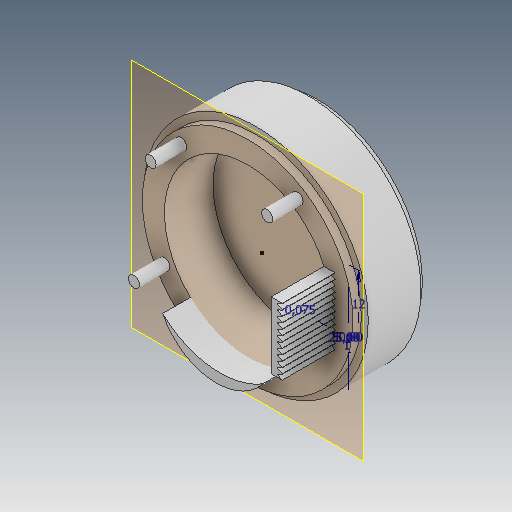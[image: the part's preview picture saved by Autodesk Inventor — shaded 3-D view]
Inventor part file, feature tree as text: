
AUTODESK INVENTOR PART (.ipt)
format: ipt  version: 2020.3 (Build 243373010, 373A)  size: 434,176 bytes
history: native  units: mm
features: extrude x11, sketch x11, plane x4, projected_geometry x3, pattern_linear x1, fillet x1
ambient origin geometry x8: Origin, YZ Plane, XZ Plane, XY Plane, X Axis, Y Axis, Z Axis, Center Point
bodies: Solid1 (feature_tree)
feature tree (31):
  extrude  "Extrusion1"  Depth=12.5mm TaperAngle=0.0deg
  extrude  "Extrusion2"  Depth=1.5mm TaperAngle=0.0deg
  extrude  "Extrusion3"  Depth=30.0mm
  extrude  "Extrusion4"  Depth=8.75mm
  extrude  "Extrusion5"  Depth=2.0mm
  plane  "Work Plane1"
  sketch  "Sketch7"  dims[d17=2.0mm d18=2.0mm]
  extrude  "Extrusion6"  Depth=2.0mm
  extrude  "Extrusion8"  Depth=12.0mm
  sketch  "Sketch10"  dims[d21=9.0mm d22=8.0mm]
  plane  "Work Plane2"
  plane  "Work Plane3"
  sketch  "Sketch14"  dims[d23=12.25mm d24=14.25mm]
  plane  "Work Plane4"
  sketch  "Sketch15"  dims[d25=5.5mm d26=0.0mm d29=10.0mm]
  extrude  "Extrusion13"  Depth=9.0mm
  extrude  "Extrusion14"  Depth=14.25mm
  extrude  "Extrusion15"  Depth=10.0mm
  pattern_linear  "Rectangular Pattern2"  Spacing1=4.363323mm  [1 undecoded]
  extrude  "Extrusion16"  Depth=1.0mm
  fillet  "Fillet1"  Radius=0.075mm
  sketch  "Sketch1"  dims[d0=40.45mm d3=12.5mm d4=0.0mm]
  sketch  "Sketch2"  dims[d6=1.25mm d7=1.5mm d8=0.0mm]
  projected_geometry  "Projected Loop1"
  sketch  "Sketch3"  dims[d9=40.45mm d10=30.0mm]
  sketch  "Sketch4"  dims[d11=8.75mm d12=0.0mm d13=1.25mm]
  sketch  "Sketch5"  dims[d14=1.5mm d15=0.0mm d16=2.0mm]
  sketch  "Sketch8"  dims[d19=15.0mm d20=12.0mm]
  projected_geometry  "Projected Loop3"
  sketch  "Sketch16"  dims[d31=12.0mm d32=3.5mm d33=0.0mm d34=4.363323mm d36=1.0mm d38=0.075mm d39=8.726646mm d40=120.0mm d42=1.0mm d43=10.0mm d45=10.0mm d49=10.75mm d50=5.0mm d51=0.0mm d53=15.0mm d54=7.5mm d59=-2.75mm d60=-20.0mm d66=7.0mm d67=0.0mm d86=0.0mm d88=120.0mm d90=10.0mm d91=12.0mm d92=4.363323mm d93=1.0mm d94=0.075mm d95=8.726646mm d96=1.0mm d97=10.0mm d98=10.0mm d99=0.0mm d100=9.5mm d101=0.0mm d102=0.415mm d111=1.104738mm d113=14.3mm d114=5.466308mm d115=2.0mm d116=0.0mm d117=100.0mm d119=11.0mm d120=0.533692mm d121=4.0mm d122=4.0mm d123=4.0mm d124=4.0mm d125=4.0mm d126=4.0mm d127=4.0mm d128=4.0mm d129=4.0mm d130=4.0mm d131=6.0mm d132=4.0mm d133=1.15mm d134=1.15mm d135=4.0mm d136=4.0mm d137=1.75mm d138=2.65mm d139=3.0mm d140=3.0mm d141=5.0mm d142=1.65mm d143=11.25mm d144=1.0mm d145=0.0mm d146=0.15mm d61=0.5mm d62=0.872665mm d87=0.872665mm d89=0.872665mm]
  projected_geometry  "Projected Loop4"
note: 1 required parameter value undecoded (feature->parameter linkage not recoverable at this tier; creation-order binding heuristic only, values carry confidence <= 0.55)
